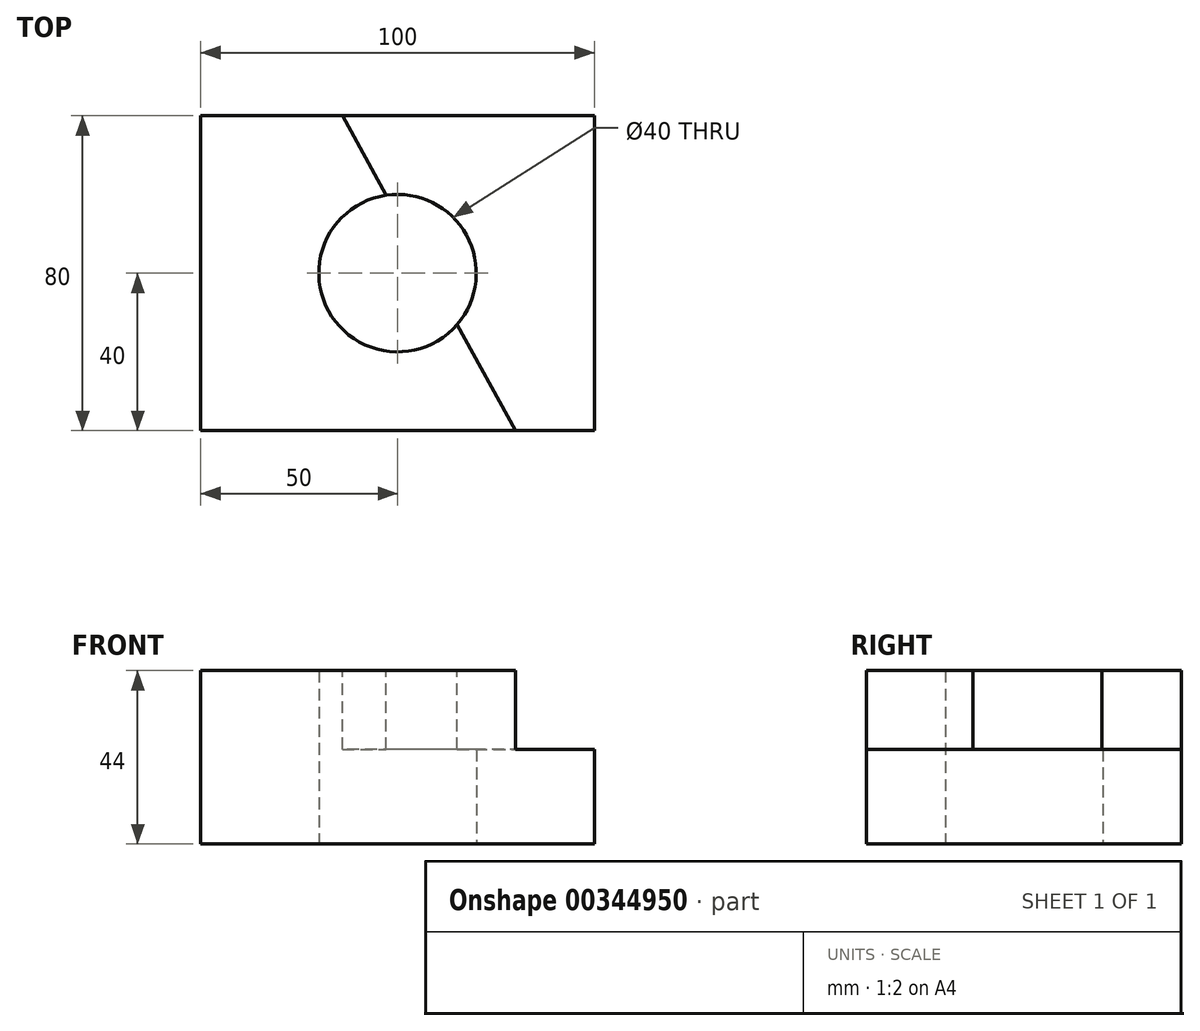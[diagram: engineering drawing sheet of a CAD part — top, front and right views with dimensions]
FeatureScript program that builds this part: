
annotation { "Feature Type Name" : "Feature", "Feature Type Description" : "" }
export const myFeature = defineFeature(function(context is Context, id is Id, definition is map)
    precondition{}
    {
        {
            var Q0;
            Q0=qCreatedBy(makeId("Top.planeOp"),FACE);
            var sketch = newSketch(context, id + "F0", { "sketchPlane" : qUnion([Q0])});
            skLineSegment(sketch, "E0.bottom", {"start": v(50, -40) * mm, "end": v(-50, -40) * mm});
            skLineSegment(sketch, "E0.top", {"start": v(50, 40) * mm, "end": v(-50, 40) * mm});
            skLineSegment(sketch, "E0.left", {"start": v(50, -40) * mm, "end": v(50, 40) * mm});
            skLineSegment(sketch, "E0.right", {"start": v(-50, -40) * mm, "end": v(-50, 40) * mm});
            skPoint(sketch, "E0.middle", {"position": v(0, 0) * mm});
            skCircle(sketch, "E1", {"center": v(0, 0) * mm, "radius": 20 * mm});
            skSolve(sketch);
        }
        {
            var Q0;
            Q0=makeQuery(id+"F0.imprint","IMPRINT",FACE,{"disambiguationData":[TD([[makeQuery(id+"F0.imprint","IMPRINT",EDGE,{"derivedFrom":sQuery(id+"F0.wireOp",EDGE,"E0.bottom")}),-1.0]])]});
            extrude(context, id + "F1", {"entities" : qUnion([Q0]), "depth" : 44 * mm});
        }
        {
            var Q0;
            Q0=makeQuery(id+"F1.opExtrude","CAP_FACE",FACE,{"disambiguationData":[OSD([sQuery(id+"F0.wireOp",EDGE,"E0.bottom"),sQuery(id+"F0.wireOp",EDGE,"E0.top"),sQuery(id+"F0.wireOp",EDGE,"E0.left"),sQuery(id+"F0.wireOp",EDGE,"E0.right"),sQuery(id+"F0.wireOp",EDGE,"E1")])],"isStart":false});
            var sketch = newSketch(context, id + "F2", { "sketchPlane" : qUnion([Q0])});
            skLineSegment(sketch, "E2", {"start": v(50, 40) * mm, "end": v(-14, 40) * mm});
            skLineSegment(sketch, "E3", {"start": v(50, -40) * mm, "end": v(30, -40) * mm});
            skLineSegment(sketch, "E4", {"start": v(50, 40) * mm, "end": v(50, -40) * mm});
            skLineSegment(sketch, "E5", {"start": v(-14, 40) * mm, "end": v(30, -40) * mm});
            skSolve(sketch);
        }
        {
            var Q0;
            {var subQ1=sQuery(id+"F2.wireOp",EDGE,"E2");Q0=makeQuery(id+"F2.imprint","IMPRINT",FACE,{"disambiguationData":[TD([[makeQuery(id+"F2.imprint","IMPRINT",EDGE,{"derivedFrom":subQ1}),1.0]])]});}
            extrude(context, id + "F3", {"entities" : qUnion([Q0]), "operationType" : NewBodyOperationType.REMOVE, "oppositeDirection" : true, "depth" : 20 * mm});
        }
    });
